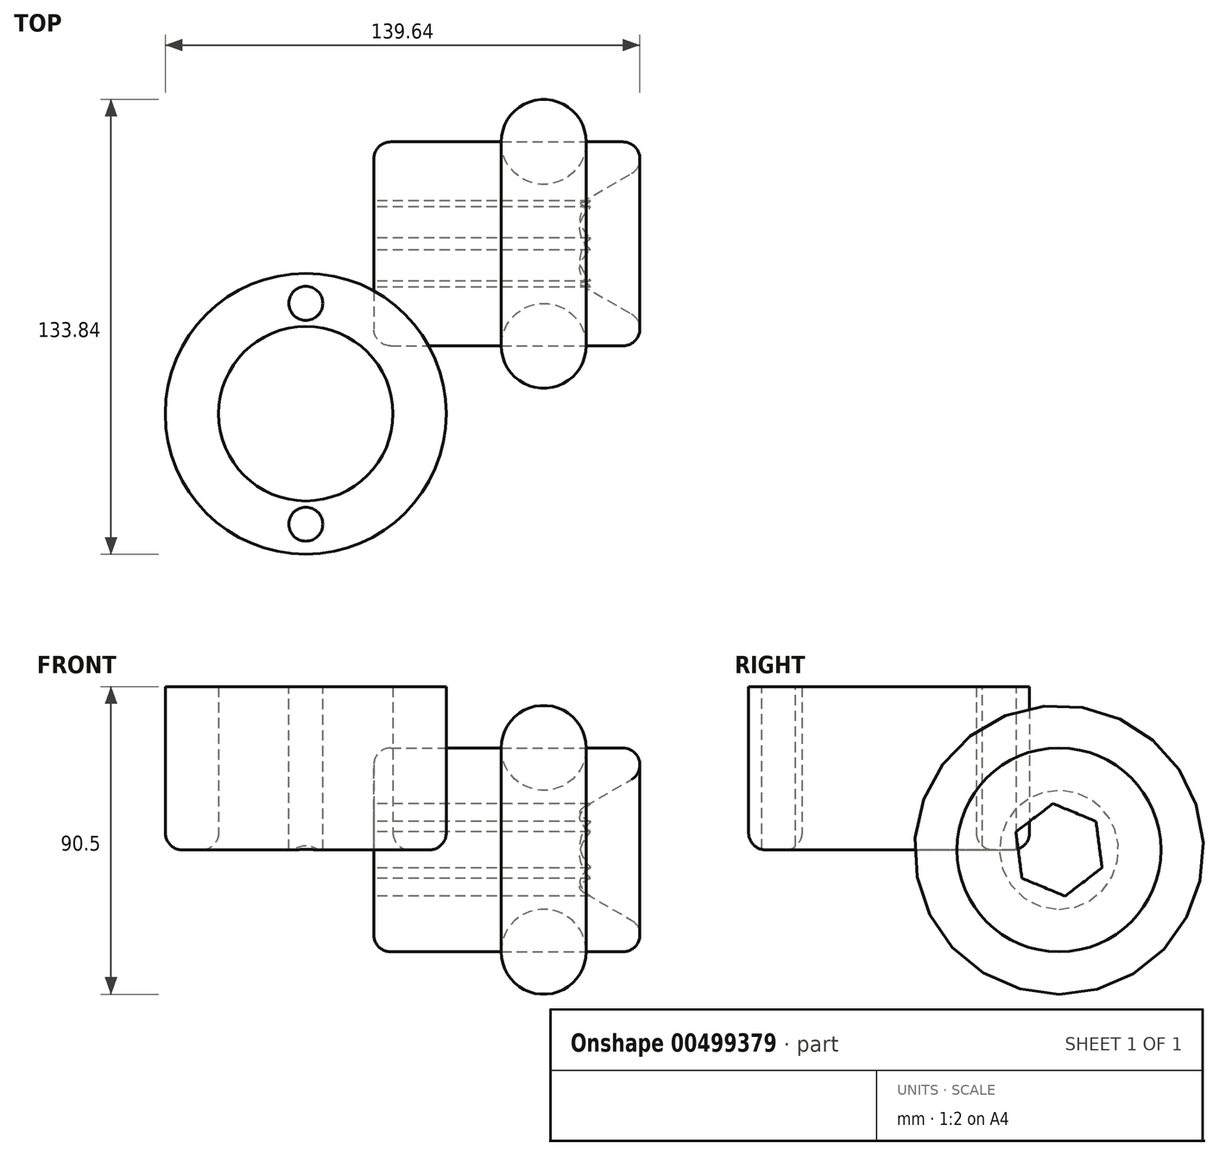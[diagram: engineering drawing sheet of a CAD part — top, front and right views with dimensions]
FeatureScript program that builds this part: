
annotation { "Feature Type Name" : "Feature", "Feature Type Description" : "" }
export const myFeature = defineFeature(function(context is Context, id is Id, definition is map)
    precondition{}
    {
        {
            var Q0;
            Q0=qCreatedBy(makeId("Top.planeOp"),FACE);
            var sketch = newSketch(context, id + "F0", { "sketchPlane" : qUnion([Q0])});
            skCircle(sketch, "E0", {"center": v(0, 0) * mm, "radius": 25.67 * mm});
            skCircle(sketch, "E1", {"center": v(0, 0) * mm, "radius": 41.34 * mm});
            skSolve(sketch);
        }
        {
            var Q0;
            Q0 = qSketchRegion(id + "F0", true);
            extrude(context, id + "F1", {"entities" : qUnion([Q0]), "depth" : 48 * mm});
        }
        {
            var Q0;
            Q0=makeQuery(id+"F1.opExtrude","CAP_FACE",FACE,{"disambiguationData":[OSD([sQuery(id+"F0.wireOp",EDGE,"E0"),sQuery(id+"F0.wireOp",EDGE,"E1")])],"isStart":false});
            var sketch = newSketch(context, id + "F2", { "sketchPlane" : qUnion([Q0])});
            skCircle(sketch, "E2", {"center": v(0, 0) * mm, "radius": 32.5 * mm});
            skCircle(sketch, "E3", {"center": v(0, 32.5) * mm, "radius": 5 * mm});
            skCircle(sketch, "E4.1.0", {"center": v(0, -32.5) * mm, "radius": 5 * mm});
            skSolve(sketch);
        }
        {
            var Q0;
            Q0=sQuery(id+"F2.wireOp",VERTEX,"E4.1.0.center");
            var Q1;
            Q1=sQuery(id+"F2.wireOp",VERTEX,"E3.center");
            var Q2;
            Q2=makeQuery(id+"F1.opExtrude","SWEPT_BODY",BODY,{"disambiguationData":[OSD([sQuery(id+"F0.wireOp",EDGE,"E0"),sQuery(id+"F0.wireOp",EDGE,"E1")])]});
            hole(context, id + "F3", {"style" : HoleStyle.SIMPLE, "endStyle" : HoleEndStyle.THROUGH, "holeDiameter" : 10 * mm, "isTappedThrough" : true, "tappedDepth" : 12 * mm, "tapClearance" : 3, "locations" : qUnion([Q0, Q1]), "scope" : qUnion([Q2])});
        }
        {
            var Q0;
            Q0=qCreatedBy(makeId("Top.planeOp"),FACE);
            var sketch = newSketch(context, id + "F4", { "sketchPlane" : qUnion([Q0])});
            skLineSegment(sketch, "E5", {"start": v(60, 50) * mm, "end": v(20, 50) * mm});
            skLineSegment(sketch, "E6", {"start": v(20, 20) * mm, "end": v(111.96, 20) * mm});
            skLineSegment(sketch, "E7", {"start": v(111.96, 20) * mm, "end": v(60, 50) * mm});
            skLineSegment(sketch, "E8", {"start": v(20, 50) * mm, "end": v(20, 20) * mm});
            skCircle(sketch, "E9", {"center": v(70, 20) * mm, "radius": 12.5 * mm});
            skSolve(sketch);
        }
        {
            var Q0;
            Q0=makeQuery(id+"F4.imprint","IMPRINT",FACE,{"disambiguationData":[TD([[makeQuery(id+"F4.imprint","IMPRINT",EDGE,{"derivedFrom":sQuery(id+"F4.wireOp",EDGE,"E5")}),1.0]])]});
            var Q1;
            {var subQ0=sQuery(id+"F4.wireOp",EDGE,"E9");var subQ1=sQuery(id+"F4.wireOp",EDGE,"E6");var subQ2=makeQuery(id+"F4.imprint","INTERSECT",VERTEX,{"disambiguationData":[OD(0.0)],"derivedFrom":[subQ1,subQ0]});Q1=makeQuery(id+"F4.imprint","IMPRINT",FACE,{"disambiguationData":[TD([[makeQuery(id+"F4.imprint","IMPRINT",EDGE,{"disambiguationData":[TD([[subQ2,-1.0]])],"derivedFrom":subQ1}),-1.0]])]});}
            var Q2;
            Q2=sQuery(id+"F4.wireOp",EDGE,"E5");
            revolve(context, id + "F5", {"entities" : qUnion([Q0, Q1]), "axis" : qUnion([Q2]), "revolveType" : RevolveType.FULL});
        }
        {
            var Q0;
            Q0=makeQuery(id+"F5.opRevolve","SWEPT_FACE",FACE,{"disambiguationData":[OSD([sQuery(id+"F4.wireOp",EDGE,"E8")])]});
            var sketch = newSketch(context, id + "F6", { "sketchPlane" : qUnion([Q0])});
            skCircle(sketch, "E10.cCircle", {"center": v(-50, 0) * mm, "radius": 11.9 * mm, "construction": true});
            skLineSegment(sketch, "E10.0", {"start": v(-51.77, -13.62) * mm, "end": v(-62.68, -5.28) * mm});
            skLineSegment(sketch, "E10.1", {"start": v(-62.68, -5.28) * mm, "end": v(-60.91, 8.34) * mm});
            skLineSegment(sketch, "E10.2", {"start": v(-60.91, 8.34) * mm, "end": v(-48.23, 13.62) * mm});
            skLineSegment(sketch, "E10.3", {"start": v(-48.23, 13.62) * mm, "end": v(-37.32, 5.28) * mm});
            skLineSegment(sketch, "E10.4", {"start": v(-37.32, 5.28) * mm, "end": v(-39.09, -8.34) * mm});
            skLineSegment(sketch, "E10.5", {"start": v(-39.09, -8.34) * mm, "end": v(-51.77, -13.62) * mm});
            skPoint(sketch, "E10.0.midPoint", {"position": v(-57.23, -9.45) * mm});
            skSolve(sketch);
        }
        {
            var Q0;
            Q0=makeQuery(id+"F6.imprint","IMPRINT",FACE,{"disambiguationData":[TD([[makeQuery(id+"F6.imprint","IMPRINT",EDGE,{"derivedFrom":sQuery(id+"F6.wireOp",EDGE,"E10.0")}),-1.0]])]});
            extrude(context, id + "F7", {"entities" : qUnion([Q0]), "operationType" : NewBodyOperationType.REMOVE, "endBound" : BoundingType.UP_TO_NEXT, "oppositeDirection" : true, "depth" : 25 * mm});
        }
        {
            var Q0;
            Q0=makeQuery(id+"F1.opExtrude","CAP_EDGE",EDGE,{"disambiguationData":[OSD([sQuery(id+"F0.wireOp",EDGE,"E1")])],"isStart":true});
            var Q1;
            Q1=makeQuery(id+"F1.opExtrude","CAP_EDGE",EDGE,{"disambiguationData":[OSD([sQuery(id+"F0.wireOp",EDGE,"E0")])],"isStart":true});
            var Q2;
            Q2=makeQuery(id+"F5.opRevolve","SWEPT_EDGE",EDGE,{"disambiguationData":[OSD([sQuery(id+"F4.wireOp",EDGE,"E6"),sQuery(id+"F4.wireOp",EDGE,"E8")])]});
            fillet(context, id + "F8", {"entities" : qUnion([Q0, Q1, Q2]), "radius" : 5 * mm, "tangentPropagation" : true, "allowEdgeOverflow" : false});
        }
        {
            var Q0;
            Q0=makeQuery(id+"F5.opRevolve","SWEPT_EDGE",EDGE,{"disambiguationData":[OSD([sQuery(id+"F4.wireOp",EDGE,"E6"),sQuery(id+"F4.wireOp",EDGE,"E7")])]});
            fillet(context, id + "F9", {"entities" : qUnion([Q0]), "radius" : 5 * mm, "tangentPropagation" : true, "allowEdgeOverflow" : false});
        }
    });
